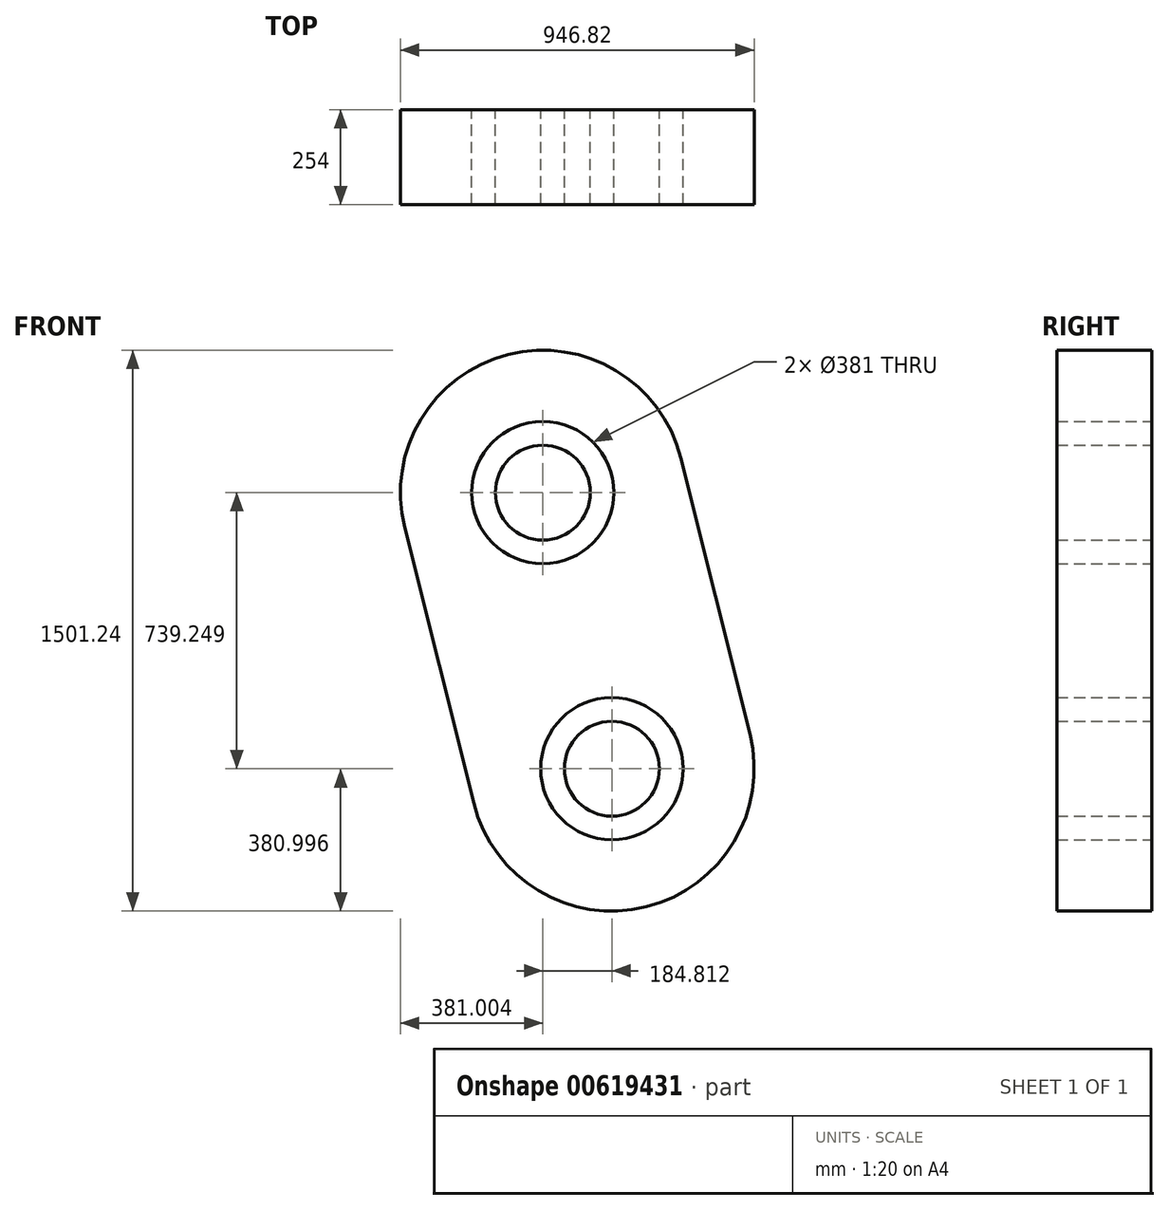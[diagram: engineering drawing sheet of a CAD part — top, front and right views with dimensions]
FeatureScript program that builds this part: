
annotation { "Feature Type Name" : "Feature", "Feature Type Description" : "" }
export const myFeature = defineFeature(function(context is Context, id is Id, definition is map)
    precondition{}
    {
        {
            var Q0;
            Q0=qCreatedBy(makeId("Front.planeOp"),FACE);
            var sketch = newSketch(context, id + "F0", { "sketchPlane" : qUnion([Q0])});
            skLineSegment(sketch, "E0.left", {"start": v(-462.03, 277.22) * mm, "end": v(-277.22, -462.03) * mm});
            skLineSegment(sketch, "E0.right", {"start": v(277.22, 462.03) * mm, "end": v(462.03, -277.22) * mm});
            skPoint(sketch, "E0.middle", {"position": v(0, 0) * mm});
            skArc(sketch, "E1", {"start": v(277.22, 462.03) * mm, "mid": v(-184.81, 739.25) * mm, "end": v(-462.03, 277.22) * mm});
            skArc(sketch, "E2", {"start": v(-277.22, -462.03) * mm, "mid": v(184.81, -739.25) * mm, "end": v(462.03, -277.22) * mm});
            skCircle(sketch, "E3", {"center": v(-92.4, 369.62) * mm, "radius": 190.5 * mm});
            skCircle(sketch, "E4", {"center": v(92.4, -369.62) * mm, "radius": 190.5 * mm});
            skLineSegment(sketch, "E5", {"start": v(-184.81, 739.25) * mm, "end": v(184.81, -739.25) * mm, "construction": true});
            skCircle(sketch, "E6", {"center": v(-92.4, 369.62) * mm, "radius": 127 * mm});
            skCircle(sketch, "E7", {"center": v(92.4, -369.62) * mm, "radius": 127 * mm});
            skSolve(sketch);
        }
        {
            var Q0;
            Q0 = qSketchRegion(id + "F0", true);
            var Q1;
            Q1=makeQuery(id+"F0.imprint","IMPRINT",FACE,{"disambiguationData":[TD([[makeQuery(id+"F0.imprint","IMPRINT",EDGE,{"derivedFrom":sQuery(id+"F0.wireOp",EDGE,"E7")}),1.0]])]});
            var Q2;
            Q2=makeQuery(id+"F0.imprint","IMPRINT",FACE,{"disambiguationData":[TD([[makeQuery(id+"F0.imprint","IMPRINT",EDGE,{"derivedFrom":sQuery(id+"F0.wireOp",EDGE,"E6")}),1.0]])]});
            extrude(context, id + "F1", {"entities" : qUnion([Q0, Q1, Q2]), "depth" : 254 * mm, "offsetDistance" : 25.4 * mm});
        }
    });
